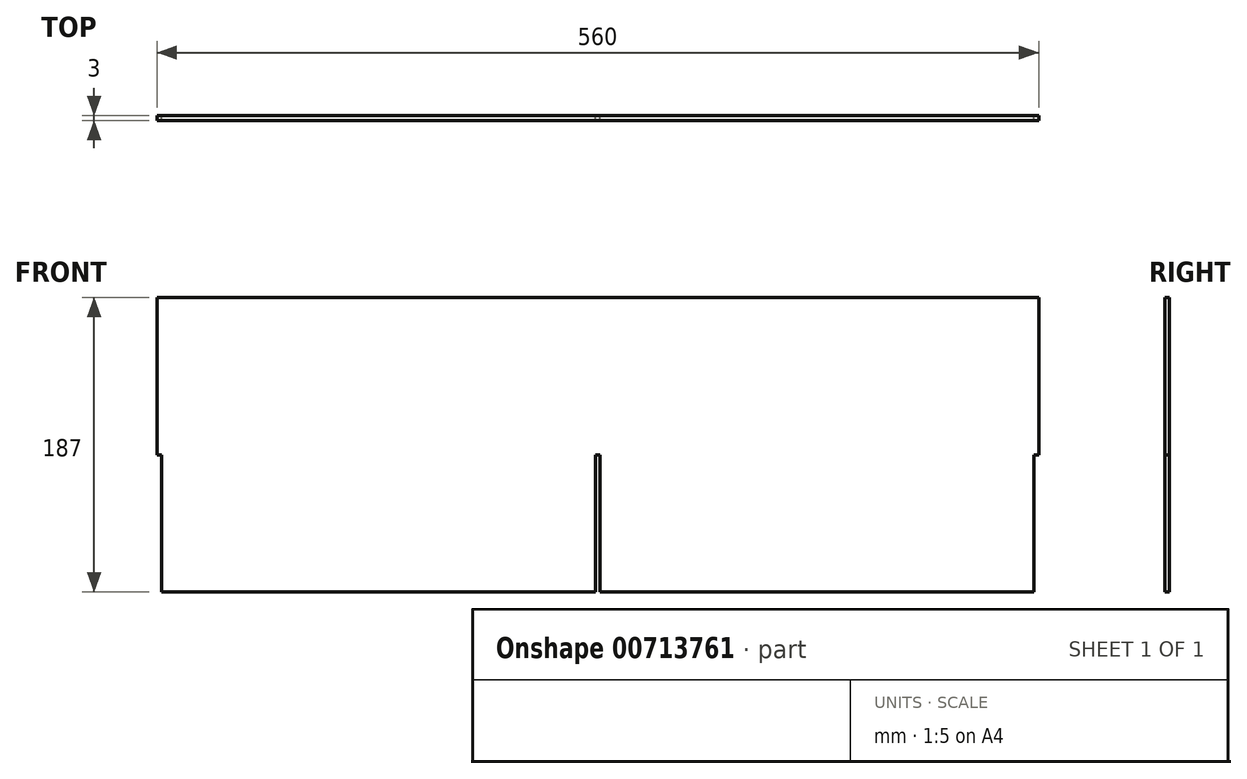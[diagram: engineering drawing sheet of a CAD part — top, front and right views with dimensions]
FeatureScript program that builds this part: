
annotation { "Feature Type Name" : "Feature", "Feature Type Description" : "" }
export const myFeature = defineFeature(function(context is Context, id is Id, definition is map)
    precondition{}
    {
        {
            var Q0;
            Q0=qCreatedBy(makeId("Front.planeOp"),FACE);
            var sketch = newSketch(context, id + "F0", { "sketchPlane" : qUnion([Q0])});
            skLineSegment(sketch, "E0.bottom", {"start": v(-280, 105) * mm, "end": v(280, 105) * mm});
            skPoint(sketch, "E0.middle", {"position": v(0, 0) * mm});
            skLineSegment(sketch, "E1.top", {"start": v(-1.5, 5) * mm, "end": v(1.5, 5) * mm});
            skLineSegment(sketch, "E1.left", {"start": v(-1.5, -82) * mm, "end": v(-1.5, 5) * mm});
            skLineSegment(sketch, "E1.right", {"start": v(1.5, -82) * mm, "end": v(1.5, 5) * mm});
            skLineSegment(sketch, "E2.top", {"start": v(-280, 5) * mm, "end": v(-277, 5) * mm});
            skLineSegment(sketch, "E2.right", {"start": v(-277, -82) * mm, "end": v(-277, 5) * mm});
            skLineSegment(sketch, "E3.top", {"start": v(280, 5) * mm, "end": v(277, 5) * mm});
            skLineSegment(sketch, "E3.right", {"start": v(277, -82) * mm, "end": v(277, 5) * mm});
            skLineSegment(sketch, "E4", {"start": v(-280, 105) * mm, "end": v(-280, 5) * mm});
            skLineSegment(sketch, "E5", {"start": v(-277, -82) * mm, "end": v(-1.5, -82) * mm});
            skLineSegment(sketch, "E6", {"start": v(1.5, -82) * mm, "end": v(277, -82) * mm});
            skLineSegment(sketch, "E7", {"start": v(280, 5) * mm, "end": v(280, 105) * mm});
            skSolve(sketch);
        }
        {
            var Q0;
            Q0=makeQuery(id+"F0.imprint","IMPRINT",FACE,{"disambiguationData":[TD([[makeQuery(id+"F0.imprint","IMPRINT",EDGE,{"derivedFrom":sQuery(id+"F0.wireOp",EDGE,"E0.bottom")}),-1.0]])]});
            extrude(context, id + "F1", {"entities" : qUnion([Q0]), "depth" : 3 * mm, "offsetDistance" : 25 * mm});
        }
    });
